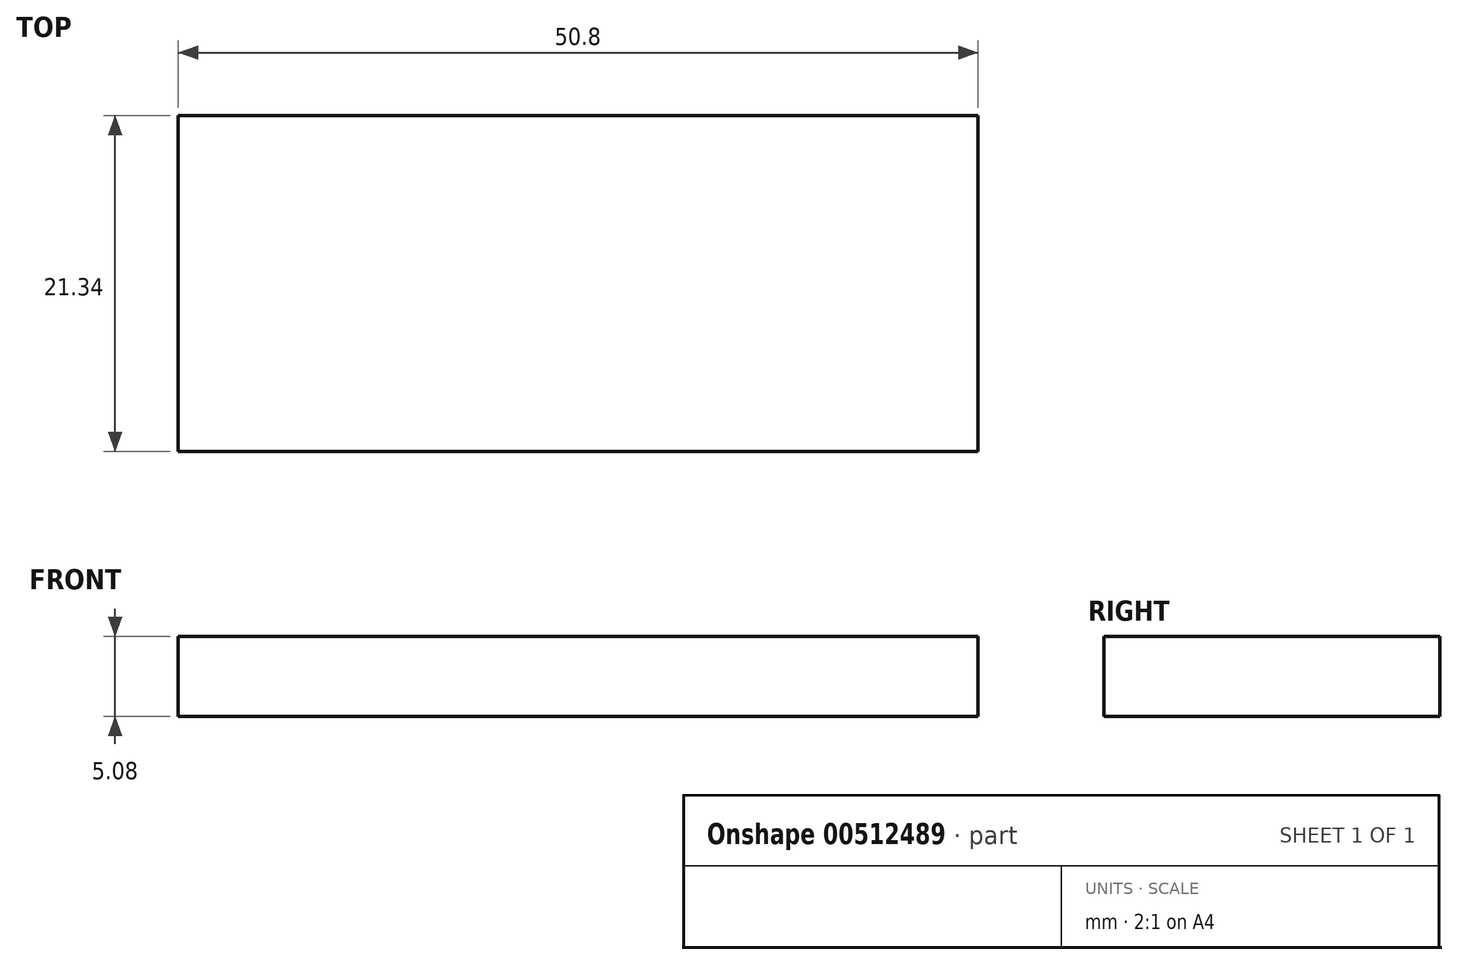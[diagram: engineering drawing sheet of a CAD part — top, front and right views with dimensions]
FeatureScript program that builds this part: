
annotation { "Feature Type Name" : "Feature", "Feature Type Description" : "" }
export const myFeature = defineFeature(function(context is Context, id is Id, definition is map)
    precondition{}
    {
        {
            var Q0;
            Q0=qCreatedBy(makeId("Top.planeOp"),FACE);
            var sketch = newSketch(context, id + "F0", { "sketchPlane" : qUnion([Q0])});
            skLineSegment(sketch, "E0.bottom", {"start": v(-21.7, 3.08) * mm, "end": v(29.1, 3.08) * mm});
            skLineSegment(sketch, "E0.top", {"start": v(-21.7, -18.26) * mm, "end": v(29.1, -18.26) * mm});
            skLineSegment(sketch, "E0.left", {"start": v(-21.7, 3.08) * mm, "end": v(-21.7, -18.26) * mm});
            skLineSegment(sketch, "E0.right", {"start": v(29.1, 3.08) * mm, "end": v(29.1, -18.26) * mm});
            skSolve(sketch);
        }
        {
            var Q0;
            Q0 = qSketchRegion(id + "F0", true);
            var Q1;
            Q1=makeQuery(id+"F0.imprint","IMPRINT",FACE,{"disambiguationData":[TD([[makeQuery(id+"F0.imprint","IMPRINT",EDGE,{"derivedFrom":sQuery(id+"F0.wireOp",EDGE,"E0.bottom")}),-1.0]])]});
            extrude(context, id + "F1", {"entities" : qUnion([Q0, Q1]), "depth" : 5.08 * mm});
        }
    });
